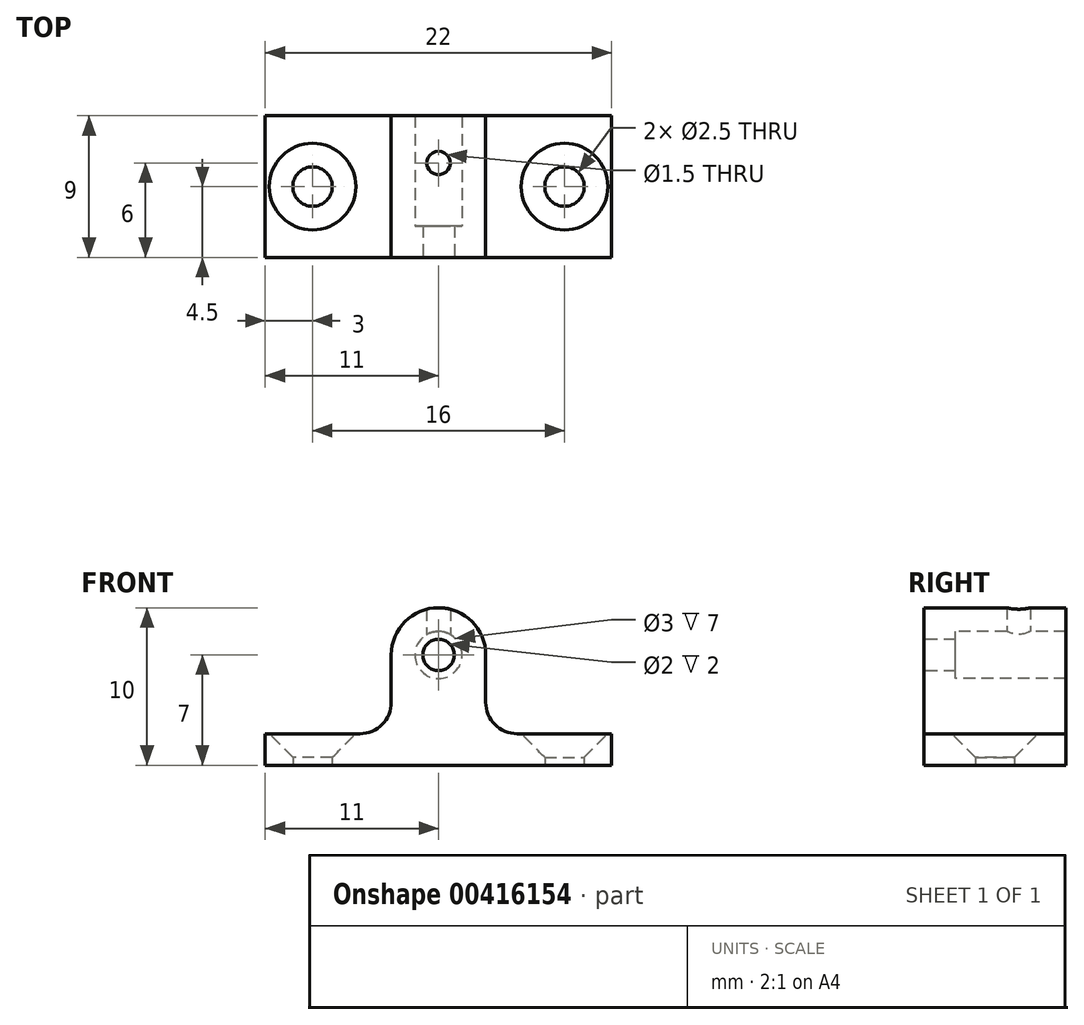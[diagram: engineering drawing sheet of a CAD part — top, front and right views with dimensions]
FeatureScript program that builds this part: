
annotation { "Feature Type Name" : "Feature", "Feature Type Description" : "" }
export const myFeature = defineFeature(function(context is Context, id is Id, definition is map)
    precondition{}
    {
        {
            var Q0;
            Q0=qCreatedBy(makeId("Front.planeOp"),FACE);
            var sketch = newSketch(context, id + "F0", { "sketchPlane" : qUnion([Q0])});
            skLineSegment(sketch, "E0.left", {"start": v(0, 0) * mm, "end": v(0, 10) * mm});
            skLineSegment(sketch, "E0.right", {"start": v(3, 4) * mm, "end": v(3, 7) * mm});
            skLineSegment(sketch, "E1.bottom", {"start": v(0, 0) * mm, "end": v(11, 0) * mm});
            skLineSegment(sketch, "E1.top", {"start": v(5, 2) * mm, "end": v(11, 2) * mm});
            skLineSegment(sketch, "E1.right", {"start": v(11, 0) * mm, "end": v(11, 2) * mm});
            skArc(sketch, "E2.filletArc", {"start": v(3, 7) * mm, "mid": v(2.12, 9.12) * mm, "end": v(0, 10) * mm});
            skLineSegment(sketch, "E3", {"start": v(0, 10) * mm, "end": v(3.04, 10) * mm, "construction": true});
            skPoint(sketch, "E4.visualSharp", {"position": v(3, 2) * mm});
            skArc(sketch, "E4.filletArc", {"start": v(3, 4) * mm, "mid": v(3.59, 2.59) * mm, "end": v(5, 2) * mm});
            skSolve(sketch);
        }
        {
            var Q0;
            Q0 = qSketchRegion(id + "F0", true);
            extrude(context, id + "F1", {"entities" : qUnion([Q0]), "depth" : 9 * mm, "offsetDistance" : 25 * mm});
        }
        {
            var Q0;
            Q0=makeQuery(id+"F1.opExtrude","SWEPT_FACE",FACE,{"disambiguationData":[OSD([sQuery(id+"F0.wireOp",EDGE,"E1.top")])]});
            var sketch = newSketch(context, id + "F2", { "sketchPlane" : qUnion([Q0])});
            skLineSegment(sketch, "E5", {"start": v(8, 0) * mm, "end": v(8, -9) * mm});
            skPoint(sketch, "E6", {"position": v(8, -4.5) * mm});
            skSolve(sketch);
        }
        {
            var Q0;
            Q0=sQuery(id+"F2.wireOp",VERTEX,"E6");
            var Q1;
            Q1=makeQuery(id+"F1.opExtrude","SWEPT_BODY",BODY,{"disambiguationData":[OSD([sQuery(id+"F0.wireOp",EDGE,"E0.left"),sQuery(id+"F0.wireOp",EDGE,"E0.right"),sQuery(id+"F0.wireOp",EDGE,"E1.bottom"),sQuery(id+"F0.wireOp",EDGE,"E1.top"),sQuery(id+"F0.wireOp",EDGE,"E1.right"),sQuery(id+"F0.wireOp",EDGE,"E2.filletArc"),sQuery(id+"F0.wireOp",EDGE,"E4.filletArc")])]});
            hole(context, id + "F3", {"style" : HoleStyle.C_SINK, "endStyle" : HoleEndStyle.THROUGH, "holeDiameter" : 2.5 * mm, "cSinkDiameter" : 5.5 * mm, "cSinkAngle" : 90 * degree, "majorDiameter" : 5 * mm, "isTappedThrough" : true, "tappedDepth" : 12 * mm, "tapClearance" : 3, "locations" : qUnion([Q0]), "scope" : qUnion([Q1])});
        }
        {
            var Q0;
            Q0=makeQuery(id+"F1.opExtrude","SWEPT_BODY",BODY,{"disambiguationData":[OSD([sQuery(id+"F0.wireOp",EDGE,"E0.left"),sQuery(id+"F0.wireOp",EDGE,"E0.right"),sQuery(id+"F0.wireOp",EDGE,"E1.bottom"),sQuery(id+"F0.wireOp",EDGE,"E1.top"),sQuery(id+"F0.wireOp",EDGE,"E1.right"),sQuery(id+"F0.wireOp",EDGE,"E2.filletArc"),sQuery(id+"F0.wireOp",EDGE,"E4.filletArc")])]});
            var Q1;
            Q1=qCreatedBy(makeId("Right.planeOp"),FACE);
            mirror(context, id + "F4", {"operationType" : NewBodyOperationType.ADD, "entities" : qUnion([Q0]), "mirrorPlane" : qUnion([Q1])});
        }
        {
            var Q0;
            Q0=sQuery(id+"F0.wireOp",VERTEX,"E2.filletArc.center");
            var Q1;
            Q1=makeQuery(id+"F1.opExtrude","SWEPT_BODY",BODY,{"disambiguationData":[OSD([sQuery(id+"F0.wireOp",EDGE,"E0.left"),sQuery(id+"F0.wireOp",EDGE,"E0.right"),sQuery(id+"F0.wireOp",EDGE,"E1.bottom"),sQuery(id+"F0.wireOp",EDGE,"E1.top"),sQuery(id+"F0.wireOp",EDGE,"E1.right"),sQuery(id+"F0.wireOp",EDGE,"E2.filletArc"),sQuery(id+"F0.wireOp",EDGE,"E4.filletArc")])]});
            hole(context, id + "F5", {"style" : HoleStyle.C_BORE, "endStyle" : HoleEndStyle.THROUGH, "oppositeDirection" : true, "holeDiameter" : 2 * mm, "cBoreDiameter" : 3 * mm, "cBoreDepth" : 7 * mm, "majorDiameter" : 5 * mm, "isTappedThrough" : true, "tappedDepth" : 12 * mm, "tapClearance" : 3, "locations" : qUnion([Q0]), "scope" : qUnion([Q1])});
        }
        {
            var Q0;
            Q0=sQuery(id+"F0.wireOp",EDGE,"E3");
            cPlane(context, id + "F6", {"entities" : qUnion([Q0]), "cplaneType" : CPlaneType.LINE_ANGLE, "offset" : 25 * mm, "angle" : 90 * degree, "width" : 150 * mm, "height" : 150 * mm});
        }
        {
            var Q0;
            Q0=qCreatedBy(id+"F6.planeOp",FACE);
            var sketch = newSketch(context, id + "F7", { "sketchPlane" : qUnion([Q0])});
            skPoint(sketch, "E7.0", {"position": v(0, 0) * mm});
            skLineSegment(sketch, "E8", {"start": v(0, 0) * mm, "end": v(0, -3) * mm});
            skPoint(sketch, "E9", {"position": v(0, -3) * mm});
            skSolve(sketch);
        }
        {
            var Q0;
            Q0=sQuery(id+"F7.wireOp",VERTEX,"E8.end");
            var Q1;
            Q1=makeQuery(id+"F1.opExtrude","SWEPT_BODY",BODY,{"disambiguationData":[OSD([sQuery(id+"F0.wireOp",EDGE,"E0.left"),sQuery(id+"F0.wireOp",EDGE,"E0.right"),sQuery(id+"F0.wireOp",EDGE,"E1.bottom"),sQuery(id+"F0.wireOp",EDGE,"E1.top"),sQuery(id+"F0.wireOp",EDGE,"E1.right"),sQuery(id+"F0.wireOp",EDGE,"E2.filletArc"),sQuery(id+"F0.wireOp",EDGE,"E4.filletArc")])]});
            hole(context, id + "F8", {"style" : HoleStyle.SIMPLE, "endStyle" : HoleEndStyle.BLIND, "holeDiameter" : 1.5 * mm, "majorDiameter" : 5 * mm, "holeDepth" : 3 * mm, "isTappedThrough" : true, "tappedDepth" : 12 * mm, "tapClearance" : 3, "locations" : qUnion([Q0]), "scope" : qUnion([Q1])});
        }
    });
